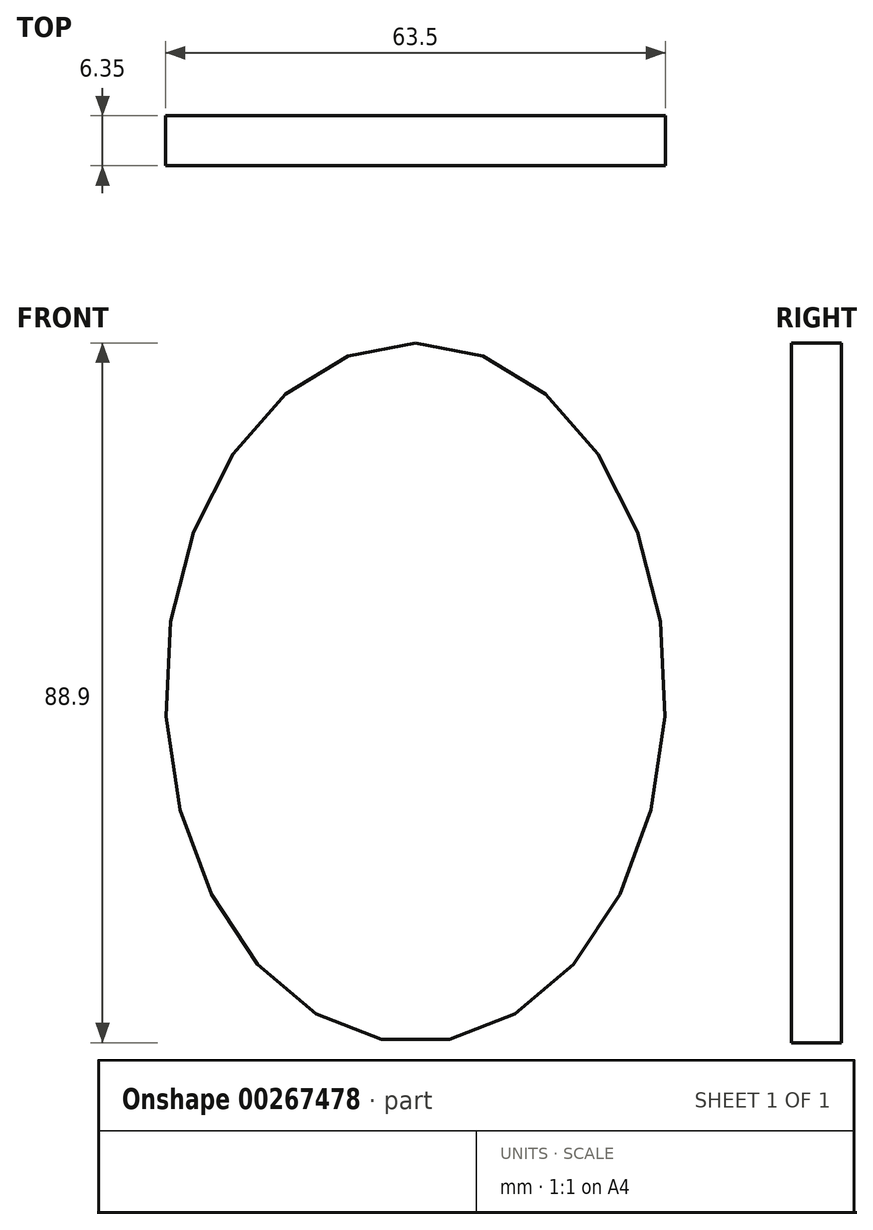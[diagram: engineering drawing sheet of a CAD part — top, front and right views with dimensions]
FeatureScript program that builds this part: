
annotation { "Feature Type Name" : "Feature", "Feature Type Description" : "" }
export const myFeature = defineFeature(function(context is Context, id is Id, definition is map)
    precondition{}
    {
        {
            var Q0;
            Q0=qCreatedBy(makeId("Front.planeOp"),FACE);
            var sketch = newSketch(context, id + "F0", { "sketchPlane" : qUnion([Q0])});
            skEllipse(sketch, "E0", {"center": v(0, 0) * mm, "majorRadius": 44.45 * mm, "minorRadius": 31.75 * mm, "majorAxis": v(0, 1)});
            skSolve(sketch);
        }
        {
            var Q0;
            Q0=makeQuery(id+"F0.imprint","IMPRINT",FACE,{"disambiguationData":[TD([[makeQuery(id+"F0.imprint","IMPRINT",EDGE,{"derivedFrom":sQuery(id+"F0.wireOp",EDGE,"E0")}),1.0]])]});
            extrude(context, id + "F1", {"entities" : qUnion([Q0]), "depth" : 6.35 * mm});
        }
    });
